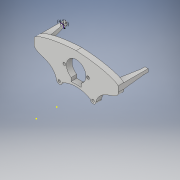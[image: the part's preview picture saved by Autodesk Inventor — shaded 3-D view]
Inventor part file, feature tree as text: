
AUTODESK INVENTOR PART (.ipt)
format: ipt  version: 2019 (Build 230136000, 136)  size: 199,168 bytes
history: native  units: mm
features: sketch x6, other x4, extrude x2, projected_geometry x2, loft x1, mirror x1
ambient origin geometry x8: Origin, YZ Plane, XZ Plane, XY Plane, X Axis, Y Axis, Z Axis, Center Point
bodies: Body1 (feature_tree)
feature tree (16):
  other  "Bryła1"
  sketch  "Szkic2"
  other  "Płaszczyzna konstrukcyjna1"
  other  "Płaszczyzna konstrukcyjna2"
  sketch  "Szkic3"
  extrude  "Wyciągnięcie proste1"  Depth=29.0mm
  sketch  "Szkic4"
  extrude  "Wyciągnięcie proste2"  Depth=4.5mm
  sketch  "Szkic6"
  sketch  "Szkic7"
  loft  "Wyciągnięcie złożone1"
  mirror  "Odbij1"
  projected_geometry  "Pętla rzutowana1"
  sketch  "Szkic5"
  projected_geometry  "Pętla rzutowana3"
  other  "Krawędzie1"
